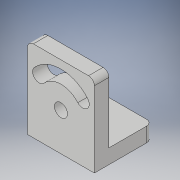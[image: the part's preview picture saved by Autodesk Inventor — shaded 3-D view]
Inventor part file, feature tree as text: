
AUTODESK INVENTOR PART (.ipt)
format: ipt  version: 2019 (Build 230136000, 136)  size: 151,040 bytes
history: native  units: mm
features: sketch x5, extrude x3, hole x2, fillet x1
ambient origin geometry x8: Origin, YZ Plane, XZ Plane, XY Plane, X Axis, Y Axis, Z Axis, Center Point
bodies: Solid1 (feature_tree)
feature tree (11):
  extrude  "Extrusion1"  Depth=28.0mm
  extrude  "Extrusion2"  Depth=5.0mm
  hole  "Hole1"  [1 undecoded]
  hole  "Hole2"  [1 undecoded]
  extrude  "Extrusion3"  Depth=2.0mm
  fillet  "Fillet1"  Radius=4.0mm
  sketch  "Sketch1"  dims[d0=23.0mm d1=28.0mm]
  sketch  "Sketch2"  dims[d2=5.0mm d3=0.0mm d4=5.0mm]
  sketch  "Sketch3"  dims[d5=15.0mm d6=0.0mm]
  sketch  "Sketch4"  dims[d7=4.496mm d8=6.0mm d9=8.433mm d10=2.0mm d11=14.3117mm d12=8.0mm d13=20.594885mm d14=8.0mm]
  sketch  "Sketch5"  dims[d15=4.496mm d16=6.0mm d17=8.433mm d18=2.0mm d19=14.3117mm d20=8.0mm d21=20.594885mm d22=20.0mm d23=4.496mm d24=4.0mm d25=10.0mm d26=0.0mm d27=2.0mm]
note: 2 required parameter values undecoded (feature->parameter linkage not recoverable at this tier; creation-order binding heuristic only, values carry confidence <= 0.55)
